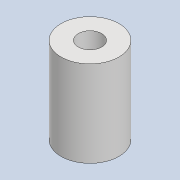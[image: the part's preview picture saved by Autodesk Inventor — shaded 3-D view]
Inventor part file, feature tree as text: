
AUTODESK INVENTOR PART (.ipt)
format: ipt  version: 2022 (Build 260153000, 153)  size: 78,336 bytes
history: native  units: in
note: dims shown in document units (in); Inventor stores cm internally (conversion verified against a paired STEP export)
features: extrude x1, sketch x1
ambient origin geometry x8: Origin, YZ Plane, XZ Plane, XY Plane, X Axis, Y Axis, Z Axis, Center Point
bodies: Solid1 (feature_tree)
feature tree (2):
  extrude  "Extrusion1"  Depth=0.625in
  sketch  "Sketch1"  dims[d0=0.208in d1=0.15in d2=0.625in d3=0.0in]
